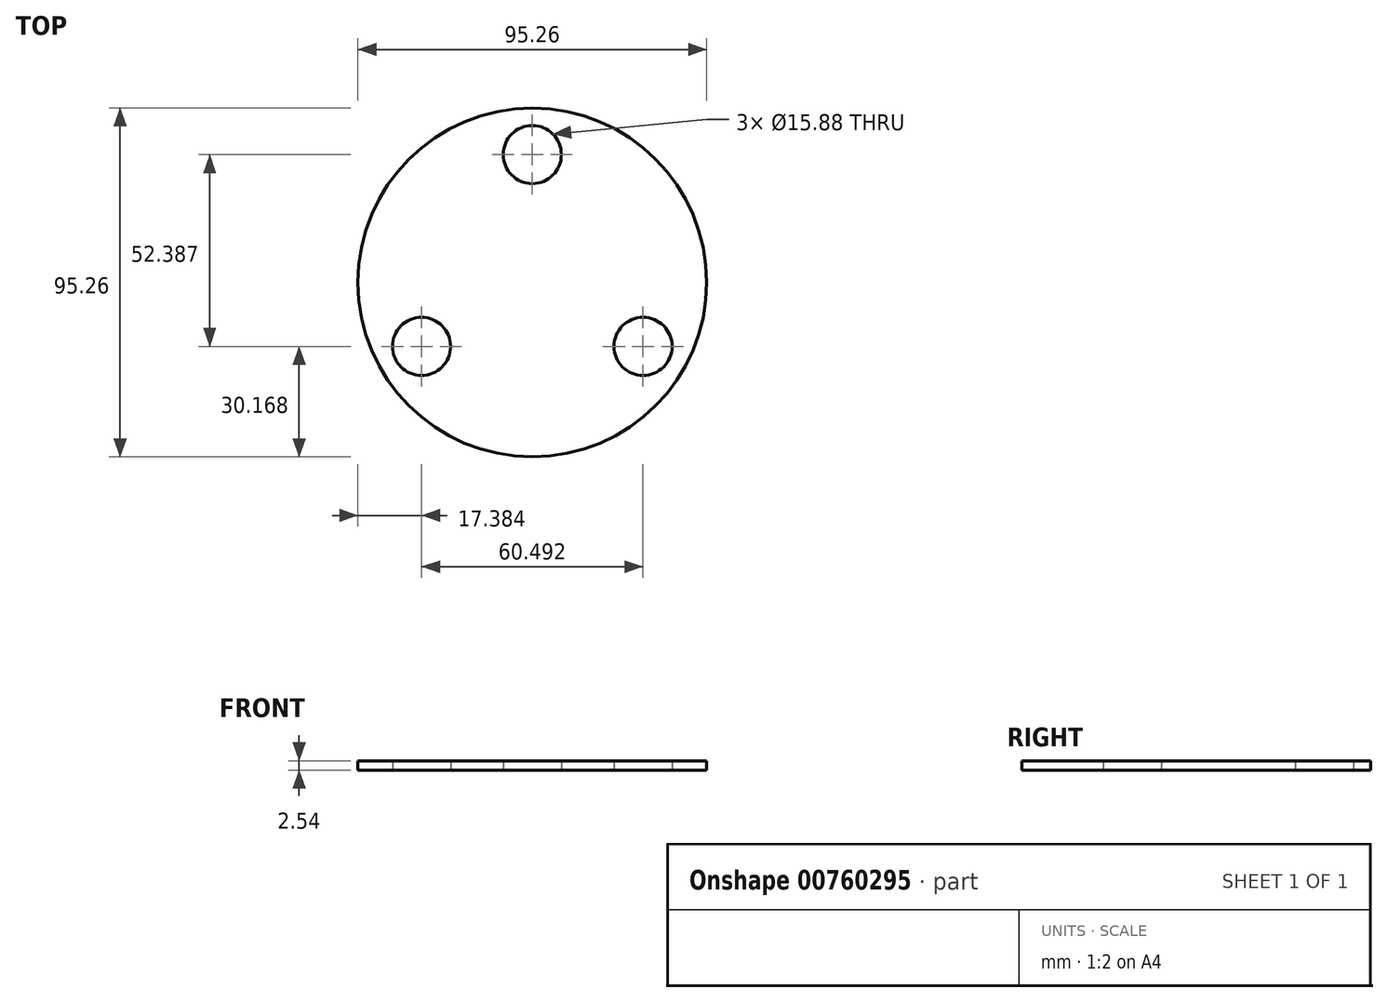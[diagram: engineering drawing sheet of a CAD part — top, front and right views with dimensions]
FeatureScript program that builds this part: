
annotation { "Feature Type Name" : "Feature", "Feature Type Description" : "" }
export const myFeature = defineFeature(function(context is Context, id is Id, definition is map)
    precondition{}
    {
        {
            var Q0;
            Q0=qCreatedBy(makeId("Top.planeOp"),FACE);
            var sketch = newSketch(context, id + "F0", { "sketchPlane" : qUnion([Q0])});
            skCircle(sketch, "E0", {"center": v(0, 0) * mm, "radius": 47.63 * mm});
            skCircle(sketch, "E1", {"center": v(0, 0) * mm, "radius": 34.93 * mm, "construction": true});
            skCircle(sketch, "E2", {"center": v(0, 34.93) * mm, "radius": 7.94 * mm});
            skCircle(sketch, "E3", {"center": v(-30.25, -17.46) * mm, "radius": 7.94 * mm});
            skCircle(sketch, "E4", {"center": v(30.25, -17.46) * mm, "radius": 7.94 * mm});
            skLineSegment(sketch, "E5", {"start": v(0, 0) * mm, "end": v(-30.25, -17.46) * mm, "construction": true});
            skLineSegment(sketch, "E6", {"start": v(0, 0) * mm, "end": v(0, 34.93) * mm, "construction": true});
            skSolve(sketch);
        }
        {
            var Q0;
            Q0=makeQuery(id+"F0.imprint","IMPRINT",FACE,{"disambiguationData":[TD([[makeQuery(id+"F0.imprint","IMPRINT",EDGE,{"derivedFrom":sQuery(id+"F0.wireOp",EDGE,"E0")}),1.0]])]});
            extrude(context, id + "F1", {"entities" : qUnion([Q0]), "depth" : 2.54 * mm, "offsetDistance" : 25.4 * mm});
        }
    });
